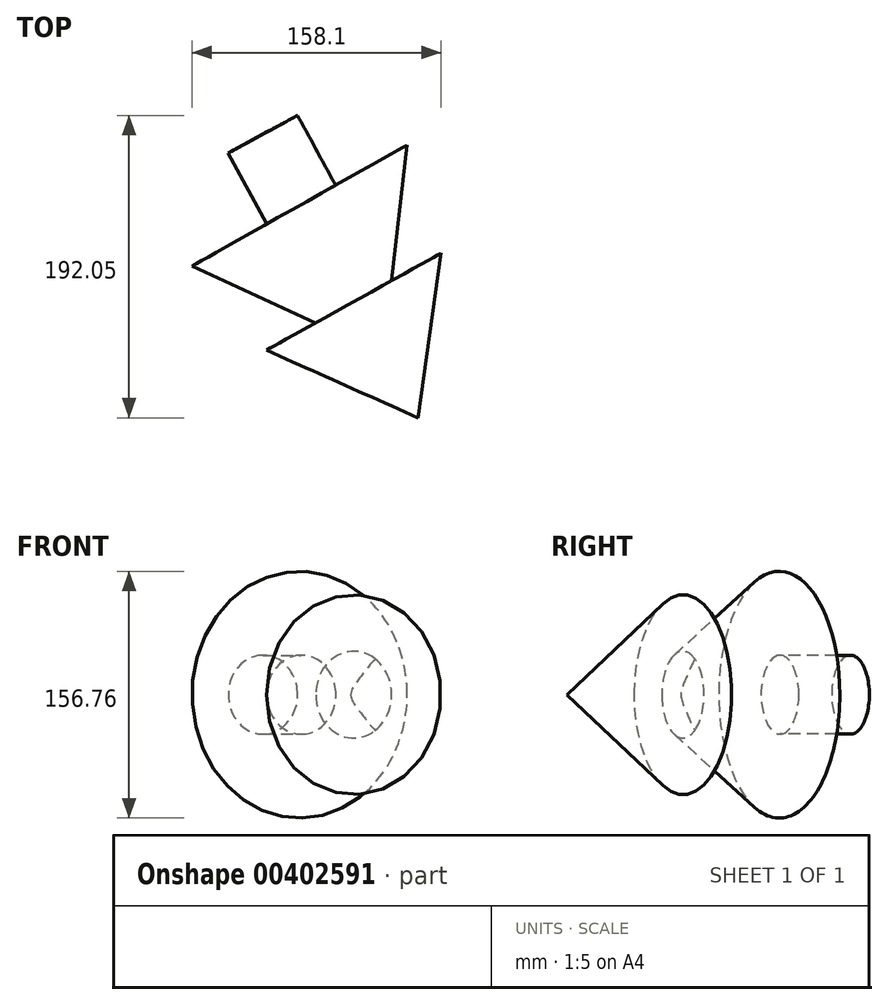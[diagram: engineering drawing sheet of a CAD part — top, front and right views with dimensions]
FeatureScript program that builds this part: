
annotation { "Feature Type Name" : "Feature", "Feature Type Description" : "" }
export const myFeature = defineFeature(function(context is Context, id is Id, definition is map)
    precondition{}
    {
        {
            var Q0;
            Q0=qCreatedBy(makeId("Top.planeOp"),FACE);
            var sketch = newSketch(context, id + "F0", { "sketchPlane" : qUnion([Q0])});
            skLineSegment(sketch, "E0", {"start": v(-64.76, 60.1) * mm, "end": v(-40.8, 73.59) * mm});
            skLineSegment(sketch, "E1", {"start": v(-40.8, 73.59) * mm, "end": v(-75.29, 134.87) * mm});
            skLineSegment(sketch, "E2", {"start": v(-75.29, 134.87) * mm, "end": v(-143.6, 96.43) * mm});
            skLineSegment(sketch, "E3", {"start": v(-64.76, 60.1) * mm, "end": v(-143.6, 96.43) * mm});
            skSolve(sketch);
        }
        {
            var Q0;
            Q0 = qSketchRegion(id + "F0", true);
            var Q1;
            Q1=sQuery(id+"F0.wireOp",EDGE,"E1");
            revolve(context, id + "F1", {"entities" : qUnion([Q0]), "axis" : qUnion([Q1]), "revolveType" : RevolveType.FULL});
        }
        {
            var Q0;
            Q0=qCreatedBy(makeId("Top.planeOp"),FACE);
            var sketch = newSketch(context, id + "F2", { "sketchPlane" : qUnion([Q0])});
            skLineSegment(sketch, "E4", {"start": v(-74.23, 135.3) * mm, "end": v(-96.24, 123.32) * mm});
            skLineSegment(sketch, "E5", {"start": v(-96.24, 123.32) * mm, "end": v(-120.6, 168.1) * mm});
            skLineSegment(sketch, "E6", {"start": v(-74.23, 135.3) * mm, "end": v(-98.73, 180.3) * mm});
            skLineSegment(sketch, "E7", {"start": v(-98.73, 180.3) * mm, "end": v(-120.6, 168.1) * mm});
            skSolve(sketch);
        }
        {
            var Q0;
            Q0=makeQuery(id+"F2.imprint","IMPRINT",FACE,{"disambiguationData":[TD([[makeQuery(id+"F2.imprint","IMPRINT",EDGE,{"derivedFrom":sQuery(id+"F2.wireOp",EDGE,"E4")}),-1.0]])]});
            var Q1;
            Q1=sQuery(id+"F2.wireOp",EDGE,"E6");
            revolve(context, id + "F3", {"entities" : qUnion([Q0]), "axis" : qUnion([Q1]), "revolveType" : RevolveType.TWO_DIRECTIONS, "angle" : 360 * degree, "angleBack" : 360 * degree});
        }
        {
            var Q0;
            Q0=qCreatedBy(makeId("Top.planeOp"),FACE);
            var sketch = newSketch(context, id + "F4", { "sketchPlane" : qUnion([Q0])});
            skLineSegment(sketch, "E8", {"start": v(-40.85, 73.54) * mm, "end": v(0, 0) * mm});
            skLineSegment(sketch, "E9", {"start": v(0, 0) * mm, "end": v(-96.45, 42.94) * mm});
            skLineSegment(sketch, "E10", {"start": v(-40.85, 73.54) * mm, "end": v(-96.45, 42.94) * mm});
            skSolve(sketch);
        }
        {
            var Q0;
            Q0 = qSketchRegion(id + "F4", true);
            var Q1;
            Q1=sQuery(id+"F4.wireOp",EDGE,"E8");
            revolve(context, id + "F5", {"operationType" : NewBodyOperationType.ADD, "entities" : qUnion([Q0]), "axis" : qUnion([Q1]), "revolveType" : RevolveType.FULL});
        }
    });
